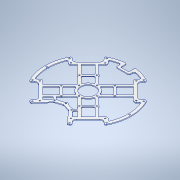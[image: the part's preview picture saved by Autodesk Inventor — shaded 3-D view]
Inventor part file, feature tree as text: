
AUTODESK INVENTOR PART (.ipt)
format: ipt  version: 2020 (Build 240168000, 168)  size: 1,146,880 bytes
history: native  units: mm
features: extrude x9, sketch x7, projected_geometry x5, other x1
ambient origin geometry x8: Origin, YZ Plane, XZ Plane, XY Plane, X Axis, Y Axis, Z Axis, Center Point
bodies: Body1 (feature_tree)
feature tree (22):
  other  "Твердое тело1"
  extrude  "outer"  TaperAngle=45.0deg  [1 undecoded]
  extrude  "inner"  Depth=7.0mm
  sketch  "Эскиз3"
  extrude  "Выдавливание3"  Depth=20.0mm
  extrude  "Выдавливание4"  Depth=7.0mm
  extrude  "Выдавливание5"  Depth=3.2mm
  sketch  "Эскиз5"
  extrude  "Выдавливание7"  Depth=59.0mm
  extrude  "Выдавливание8"  Depth=83.0mm
  sketch  "Эскиз6"
  extrude  "Выдавливание9"  Depth=69.0mm
  extrude  "Выдавливание10"  Depth=55.0mm
  sketch  "Эскиз7"
  sketch  "Эскиз1"
  sketch  "Эскиз2"
  projected_geometry  "Спроецированная петля1"
  projected_geometry  "Спроецированная петля2"
  sketch  "Эскиз4"
  projected_geometry  "Спроецированная петля3"
  projected_geometry  "Спроецированная петля4"
  projected_geometry  "Спроецированная петля5"
note: 1 required parameter value undecoded (feature->parameter linkage not recoverable at this tier; creation-order binding heuristic only, values carry confidence <= 0.55)
